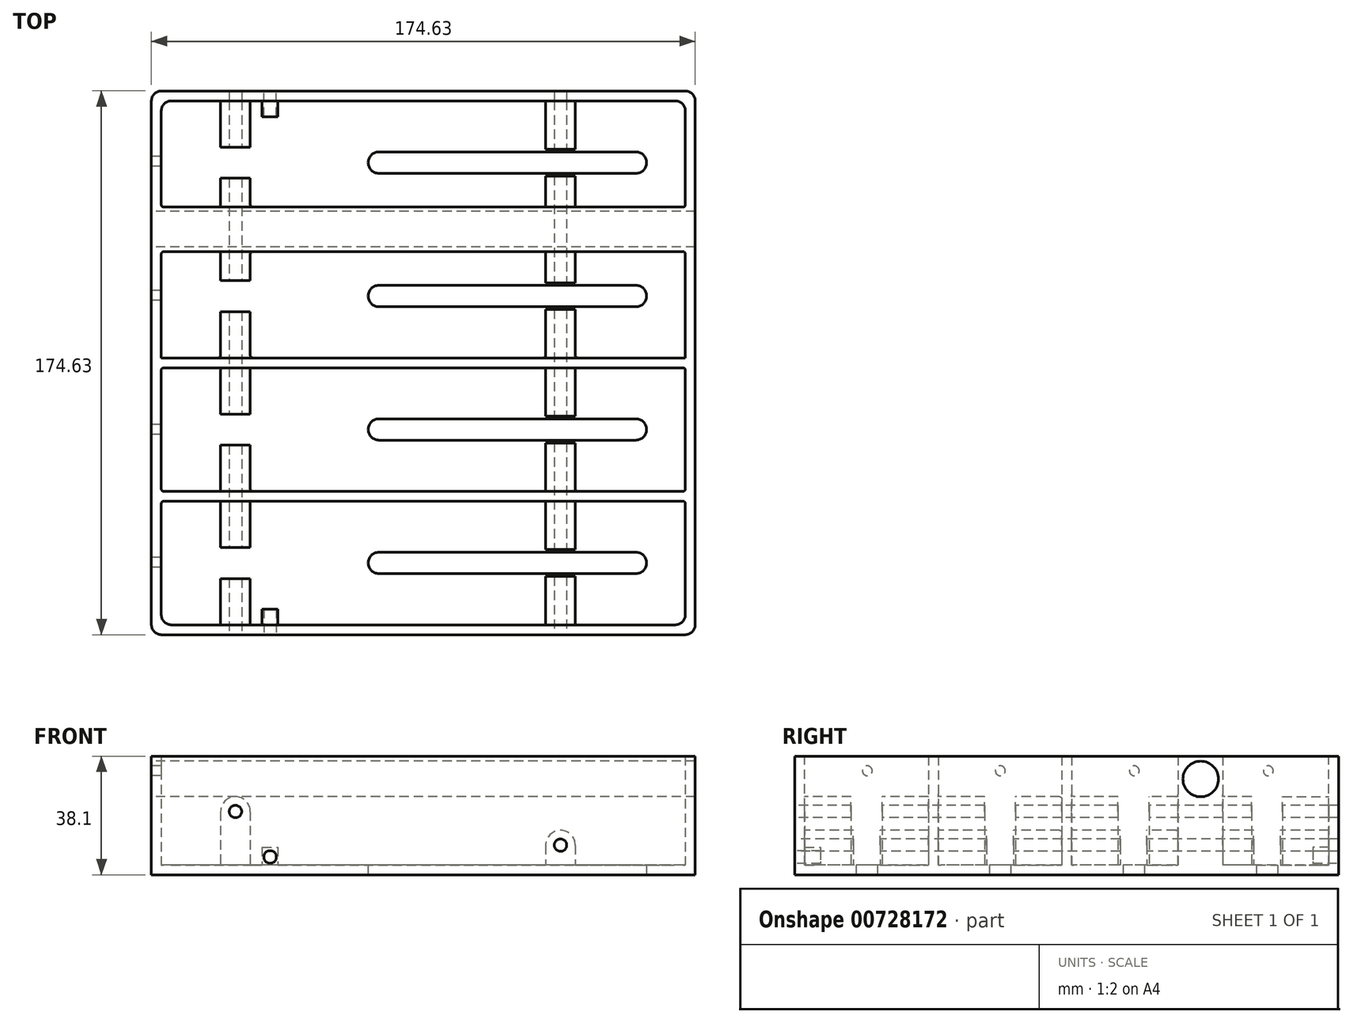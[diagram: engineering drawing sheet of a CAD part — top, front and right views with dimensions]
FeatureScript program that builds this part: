
annotation { "Feature Type Name" : "Feature", "Feature Type Description" : "" }
export const myFeature = defineFeature(function(context is Context, id is Id, definition is map)
    precondition{}
    {
        {
            var Q0;
            Q0=qCreatedBy(makeId("Top.planeOp"),FACE);
            var sketch = newSketch(context, id + "F0", { "sketchPlane" : qUnion([Q0])});
            skLineSegment(sketch, "E0.bottom", {"start": v(0, 0) * mm, "end": v(174.63, 0) * mm});
            skLineSegment(sketch, "E0.top", {"start": v(0, 174.63) * mm, "end": v(174.62, 174.63) * mm});
            skLineSegment(sketch, "E0.left", {"start": v(0, 0) * mm, "end": v(0, 174.63) * mm});
            skLineSegment(sketch, "E0.right", {"start": v(174.63, 0) * mm, "end": v(174.62, 174.63) * mm});
            skSolve(sketch);
        }
        {
            var Q0;
            Q0=qSketchRegion(id+"F0",true);
            extrude(context, id + "F1", {"entities" : qUnion([Q0]), "depth" : 38.1 * mm, "offsetDistance" : 25.4 * mm});
        }
        {
            var Q0;
            Q0=makeQuery(id+"F1.opExtrude","CAP_FACE",FACE,{"disambiguationData":[OSD([sQuery(id+"F0.wireOp",EDGE,"E0.bottom"),sQuery(id+"F0.wireOp",EDGE,"E0.top"),sQuery(id+"F0.wireOp",EDGE,"E0.left"),sQuery(id+"F0.wireOp",EDGE,"E0.right")])],"isStart":false});
            var sketch = newSketch(context, id + "F2", { "sketchPlane" : qUnion([Q0])});
            skLineSegment(sketch, "E1.bottom", {"start": v(3.17, 171.45) * mm, "end": v(171.45, 171.45) * mm});
            skLineSegment(sketch, "E1.top", {"start": v(3.18, 3.18) * mm, "end": v(171.45, 3.18) * mm});
            skLineSegment(sketch, "E1.left", {"start": v(3.17, 171.45) * mm, "end": v(3.18, 3.17) * mm});
            skLineSegment(sketch, "E1.right", {"start": v(171.45, 171.45) * mm, "end": v(171.45, 3.18) * mm});
            skSolve(sketch);
        }
        {
            var Q0;
            Q0=qSketchRegion(id+"F2",true);
            extrude(context, id + "F3", {"entities" : qUnion([Q0]), "operationType" : NewBodyOperationType.REMOVE, "oppositeDirection" : true, "depth" : 34.92 * mm, "offsetDistance" : 25.4 * mm});
        }
        {
            var Q0;
            Q0=makeQuery(id+"F3.boolean.opBoolean","COPY",EDGE,{"derivedFrom":makeQuery(id+"F3.opExtrude","SWEPT_EDGE",EDGE,{"disambiguationData":[OSD([sQuery(id+"F2.wireOp",EDGE,"E1.bottom"),sQuery(id+"F2.wireOp",EDGE,"E1.right")])]})});
            var Q1;
            Q1=makeQuery(id+"F3.boolean.opBoolean","COPY",EDGE,{"derivedFrom":makeQuery(id+"F3.opExtrude","SWEPT_EDGE",EDGE,{"disambiguationData":[OSD([sQuery(id+"F2.wireOp",EDGE,"E1.top"),sQuery(id+"F2.wireOp",EDGE,"E1.right")])]})});
            var Q2;
            Q2=makeQuery(id+"F3.boolean.opBoolean","COPY",EDGE,{"derivedFrom":makeQuery(id+"F3.opExtrude","SWEPT_EDGE",EDGE,{"disambiguationData":[OSD([sQuery(id+"F2.wireOp",EDGE,"E1.bottom"),sQuery(id+"F2.wireOp",EDGE,"E1.left")])]})});
            var Q3;
            Q3=makeQuery(id+"F3.boolean.opBoolean","COPY",EDGE,{"derivedFrom":makeQuery(id+"F3.opExtrude","SWEPT_EDGE",EDGE,{"disambiguationData":[OSD([sQuery(id+"F2.wireOp",EDGE,"E1.top"),sQuery(id+"F2.wireOp",EDGE,"E1.left")])]})});
            var Q4;
            Q4=makeQuery(id+"F1.opExtrude","SWEPT_EDGE",EDGE,{"disambiguationData":[OSD([sQuery(id+"F0.wireOp",EDGE,"E0.top"),sQuery(id+"F0.wireOp",EDGE,"E0.right")])]});
            var Q5;
            Q5=makeQuery(id+"F1.opExtrude","SWEPT_EDGE",EDGE,{"disambiguationData":[OSD([sQuery(id+"F0.wireOp",EDGE,"E0.top"),sQuery(id+"F0.wireOp",EDGE,"E0.left")])]});
            var Q6;
            Q6=makeQuery(id+"F1.opExtrude","SWEPT_EDGE",EDGE,{"disambiguationData":[OSD([sQuery(id+"F0.wireOp",EDGE,"E0.bottom"),sQuery(id+"F0.wireOp",EDGE,"E0.right")])]});
            var Q7;
            Q7=makeQuery(id+"F1.opExtrude","SWEPT_EDGE",EDGE,{"disambiguationData":[OSD([sQuery(id+"F0.wireOp",EDGE,"E0.bottom"),sQuery(id+"F0.wireOp",EDGE,"E0.left")])]});
            fillet(context, id + "F4", {"entities" : qUnion([Q0, Q1, Q2, Q3, Q4, Q5, Q6, Q7]), "radius" : 3.17 * mm, "tangentPropagation" : true, "allowEdgeOverflow" : false});
        }
        {
            var Q0;
            Q0=qCreatedBy(makeId("Top.planeOp"),FACE);
            var sketch = newSketch(context, id + "F5", { "sketchPlane" : qUnion([Q0])});
            skLineSegment(sketch, "E2.bottom", {"start": v(3.36, 131.76) * mm, "end": v(171.33, 131.76) * mm});
            skLineSegment(sketch, "E2.top", {"start": v(3.36, 128.59) * mm, "end": v(171.33, 128.59) * mm});
            skLineSegment(sketch, "E2.left", {"start": v(3.36, 131.76) * mm, "end": v(3.36, 128.59) * mm});
            skLineSegment(sketch, "E2.right", {"start": v(171.33, 131.76) * mm, "end": v(171.33, 128.59) * mm});
            skLineSegment(sketch, "E3.bottom", {"start": v(3.17, 88.9) * mm, "end": v(171.45, 88.9) * mm});
            skLineSegment(sketch, "E3.top", {"start": v(3.17, 85.72) * mm, "end": v(171.45, 85.72) * mm});
            skLineSegment(sketch, "E3.left", {"start": v(3.17, 88.9) * mm, "end": v(3.17, 85.72) * mm});
            skLineSegment(sketch, "E3.right", {"start": v(171.45, 88.9) * mm, "end": v(171.45, 85.73) * mm});
            skLineSegment(sketch, "E4.bottom", {"start": v(3.18, 46.04) * mm, "end": v(171.45, 46.04) * mm});
            skLineSegment(sketch, "E4.top", {"start": v(3.18, 42.86) * mm, "end": v(171.45, 42.86) * mm});
            skLineSegment(sketch, "E4.left", {"start": v(3.18, 46.04) * mm, "end": v(3.18, 42.86) * mm});
            skLineSegment(sketch, "E4.right", {"start": v(171.45, 46.04) * mm, "end": v(171.45, 42.86) * mm});
            skSolve(sketch);
        }
        {
            var Q0;
            Q0=qSketchRegion(id+"F5",true);
            extrude(context, id + "F6", {"entities" : qUnion([Q0]), "operationType" : NewBodyOperationType.ADD, "depth" : 38.1 * mm, "offsetDistance" : 25.4 * mm});
        }
        {
            var Q0;
            Q0=qCreatedBy(makeId("Top.planeOp"),FACE);
            var sketch = newSketch(context, id + "F7", { "sketchPlane" : qUnion([Q0])});
            skLineSegment(sketch, "E5", {"start": v(73.02, 155.03) * mm, "end": v(155.57, 155.03) * mm});
            skArc(sketch, "E6", {"start": v(155.57, 148.17) * mm, "mid": v(159, 151.6) * mm, "end": v(155.57, 155.03) * mm});
            skLineSegment(sketch, "E7", {"start": v(155.57, 148.17) * mm, "end": v(73.02, 148.17) * mm});
            skArc(sketch, "E8", {"start": v(73.02, 155.03) * mm, "mid": v(69.6, 151.6) * mm, "end": v(73.02, 148.17) * mm});
            skLineSegment(sketch, "E9.0.1.0", {"start": v(155.57, 105.32) * mm, "end": v(73.02, 105.32) * mm});
            skArc(sketch, "E9.0.1.1", {"start": v(155.57, 105.32) * mm, "mid": v(159, 108.75) * mm, "end": v(155.57, 112.18) * mm});
            skLineSegment(sketch, "E9.0.1.2", {"start": v(73.02, 112.18) * mm, "end": v(155.57, 112.18) * mm});
            skArc(sketch, "E9.0.1.3", {"start": v(73.02, 112.18) * mm, "mid": v(69.6, 108.75) * mm, "end": v(73.02, 105.32) * mm});
            skLineSegment(sketch, "E9.0.2.0", {"start": v(155.57, 62.47) * mm, "end": v(73.02, 62.47) * mm});
            skArc(sketch, "E9.0.2.1", {"start": v(155.57, 62.47) * mm, "mid": v(159, 65.9) * mm, "end": v(155.57, 69.33) * mm});
            skLineSegment(sketch, "E9.0.2.2", {"start": v(73.02, 69.33) * mm, "end": v(155.57, 69.33) * mm});
            skArc(sketch, "E9.0.2.3", {"start": v(73.02, 69.33) * mm, "mid": v(69.6, 65.9) * mm, "end": v(73.02, 62.47) * mm});
            skLineSegment(sketch, "E9.0.3.0", {"start": v(155.57, 19.62) * mm, "end": v(73.02, 19.62) * mm});
            skArc(sketch, "E9.0.3.1", {"start": v(155.57, 19.62) * mm, "mid": v(159, 23.05) * mm, "end": v(155.57, 26.48) * mm});
            skLineSegment(sketch, "E9.0.3.2", {"start": v(73.02, 26.48) * mm, "end": v(155.57, 26.48) * mm});
            skArc(sketch, "E9.0.3.3", {"start": v(73.02, 26.48) * mm, "mid": v(69.6, 23.05) * mm, "end": v(73.02, 19.62) * mm});
            skLineSegment(sketch, "E9.direction1", {"start": v(73.02, 148.17) * mm, "end": v(73.02, 148.17) * mm});
            skLineSegment(sketch, "E9.direction2", {"start": v(73.02, 148.17) * mm, "end": v(73.02, 105.32) * mm, "construction": true});
            skSolve(sketch);
        }
        {
            var Q0;
            Q0=qSketchRegion(id+"F7",true);
            extrude(context, id + "F8", {"entities" : qUnion([Q0]), "operationType" : NewBodyOperationType.REMOVE, "depth" : 5.08 * mm, "offsetDistance" : 25.4 * mm});
        }
        {
            var Q0;
            Q0=makeQuery(id+"F1.opExtrude","SWEPT_FACE",FACE,{"disambiguationData":[OSD([sQuery(id+"F0.wireOp",EDGE,"E0.bottom")])]});
            var sketch = newSketch(context, id + "F9", { "sketchPlane" : qUnion([Q0])});
            skCircle(sketch, "E10", {"center": v(131.36, 9.53) * mm, "radius": 2 * mm});
            skCircle(sketch, "E11", {"center": v(26.99, 20.32) * mm, "radius": 2 * mm});
            skSolve(sketch);
        }
        {
            var Q0;
            Q0=qCreatedBy(makeId("Top.planeOp"),FACE);
            var sketch = newSketch(context, id + "F10", { "sketchPlane" : qUnion([Q0])});
            skLineSegment(sketch, "E12.bottom", {"start": v(22.23, 3.18) * mm, "end": v(31.75, 3.18) * mm});
            skLineSegment(sketch, "E12.top", {"start": v(22.23, 18.03) * mm, "end": v(31.75, 18.03) * mm});
            skLineSegment(sketch, "E12.left", {"start": v(22.23, 3.18) * mm, "end": v(22.23, 18.03) * mm});
            skLineSegment(sketch, "E12.right", {"start": v(31.75, 3.18) * mm, "end": v(31.75, 18.03) * mm});
            skLineSegment(sketch, "E13.bottom", {"start": v(22.23, 42.86) * mm, "end": v(31.75, 42.86) * mm});
            skLineSegment(sketch, "E13.top", {"start": v(22.23, 28) * mm, "end": v(31.75, 28) * mm});
            skLineSegment(sketch, "E13.left", {"start": v(22.23, 42.86) * mm, "end": v(22.23, 28) * mm});
            skLineSegment(sketch, "E13.right", {"start": v(31.75, 42.86) * mm, "end": v(31.75, 28) * mm});
            skLineSegment(sketch, "E14.0.1.0", {"start": v(31.75, 46.02) * mm, "end": v(31.75, 60.88) * mm});
            skLineSegment(sketch, "E14.0.1.1", {"start": v(22.23, 60.88) * mm, "end": v(31.75, 60.88) * mm});
            skLineSegment(sketch, "E14.0.1.2", {"start": v(22.23, 46.02) * mm, "end": v(22.23, 60.88) * mm});
            skLineSegment(sketch, "E14.0.1.3", {"start": v(22.23, 46.02) * mm, "end": v(31.75, 46.02) * mm});
            skLineSegment(sketch, "E14.0.1.4", {"start": v(22.23, 70.85) * mm, "end": v(31.75, 70.85) * mm});
            skLineSegment(sketch, "E14.0.1.5", {"start": v(31.75, 85.71) * mm, "end": v(31.75, 70.85) * mm});
            skLineSegment(sketch, "E14.0.1.6", {"start": v(22.23, 85.71) * mm, "end": v(22.23, 70.85) * mm});
            skLineSegment(sketch, "E14.0.1.7", {"start": v(22.23, 85.71) * mm, "end": v(31.75, 85.71) * mm});
            skLineSegment(sketch, "E14.0.2.0", {"start": v(31.75, 88.87) * mm, "end": v(31.75, 103.73) * mm});
            skLineSegment(sketch, "E14.0.2.1", {"start": v(22.23, 103.73) * mm, "end": v(31.75, 103.73) * mm});
            skLineSegment(sketch, "E14.0.2.2", {"start": v(22.23, 88.87) * mm, "end": v(22.23, 103.73) * mm});
            skLineSegment(sketch, "E14.0.2.3", {"start": v(22.23, 88.87) * mm, "end": v(31.75, 88.87) * mm});
            skLineSegment(sketch, "E14.0.2.4", {"start": v(22.23, 113.7) * mm, "end": v(31.75, 113.7) * mm});
            skLineSegment(sketch, "E14.0.2.5", {"start": v(31.75, 128.56) * mm, "end": v(31.75, 113.7) * mm});
            skLineSegment(sketch, "E14.0.2.6", {"start": v(22.23, 128.56) * mm, "end": v(22.23, 113.7) * mm});
            skLineSegment(sketch, "E14.0.2.7", {"start": v(22.23, 128.56) * mm, "end": v(31.75, 128.56) * mm});
            skLineSegment(sketch, "E14.0.3.0", {"start": v(31.75, 131.72) * mm, "end": v(31.75, 146.58) * mm});
            skLineSegment(sketch, "E14.0.3.1", {"start": v(22.23, 146.58) * mm, "end": v(31.75, 146.58) * mm});
            skLineSegment(sketch, "E14.0.3.2", {"start": v(22.23, 131.72) * mm, "end": v(22.23, 146.58) * mm});
            skLineSegment(sketch, "E14.0.3.3", {"start": v(22.23, 131.72) * mm, "end": v(31.75, 131.72) * mm});
            skLineSegment(sketch, "E14.0.3.4", {"start": v(22.23, 156.55) * mm, "end": v(31.75, 156.55) * mm});
            skLineSegment(sketch, "E14.0.3.5", {"start": v(31.75, 171.41) * mm, "end": v(31.75, 156.55) * mm});
            skLineSegment(sketch, "E14.0.3.6", {"start": v(22.23, 171.41) * mm, "end": v(22.23, 156.55) * mm});
            skLineSegment(sketch, "E14.0.3.7", {"start": v(22.23, 171.41) * mm, "end": v(31.75, 171.41) * mm});
            skLineSegment(sketch, "E14.direction1", {"start": v(31.75, 3.18) * mm, "end": v(31.75, 3.18) * mm});
            skSolve(sketch);
        }
        {
            var Q0;
            Q0=qSketchRegion(id+"F10",true);
            extrude(context, id + "F11", {"entities" : qUnion([Q0]), "operationType" : NewBodyOperationType.ADD, "depth" : 25.1 * mm, "offsetDistance" : 25.4 * mm});
        }
        {
            var Q0;
            Q0=makeQuery(id+"F11.opExtrude","CAP_EDGE",EDGE,{"disambiguationData":[OSD([sQuery(id+"F10.wireOp",EDGE,"E14.0.3.6")])],"isStart":false});
            var Q1;
            Q1=makeQuery(id+"F11.opExtrude","CAP_EDGE",EDGE,{"disambiguationData":[OSD([sQuery(id+"F10.wireOp",EDGE,"E14.0.3.5")])],"isStart":false});
            var Q2;
            Q2=makeQuery(id+"F11.opExtrude","CAP_EDGE",EDGE,{"disambiguationData":[OSD([sQuery(id+"F10.wireOp",EDGE,"E14.0.3.0")])],"isStart":false});
            var Q3;
            Q3=makeQuery(id+"F11.opExtrude","CAP_EDGE",EDGE,{"disambiguationData":[OSD([sQuery(id+"F10.wireOp",EDGE,"E14.0.3.2")])],"isStart":false});
            var Q4;
            Q4=makeQuery(id+"F11.opExtrude","CAP_EDGE",EDGE,{"disambiguationData":[OSD([sQuery(id+"F10.wireOp",EDGE,"E14.0.2.5")])],"isStart":false});
            var Q5;
            Q5=makeQuery(id+"F11.opExtrude","CAP_EDGE",EDGE,{"disambiguationData":[OSD([sQuery(id+"F10.wireOp",EDGE,"E14.0.2.0")])],"isStart":false});
            var Q6;
            Q6=makeQuery(id+"F11.opExtrude","CAP_EDGE",EDGE,{"disambiguationData":[OSD([sQuery(id+"F10.wireOp",EDGE,"E14.0.1.5")])],"isStart":false});
            var Q7;
            Q7=makeQuery(id+"F11.opExtrude","CAP_EDGE",EDGE,{"disambiguationData":[OSD([sQuery(id+"F10.wireOp",EDGE,"E14.0.1.0")])],"isStart":false});
            var Q8;
            Q8=makeQuery(id+"F11.opExtrude","CAP_EDGE",EDGE,{"disambiguationData":[OSD([sQuery(id+"F10.wireOp",EDGE,"E13.right")])],"isStart":false});
            var Q9;
            Q9=makeQuery(id+"F11.opExtrude","CAP_EDGE",EDGE,{"disambiguationData":[OSD([sQuery(id+"F10.wireOp",EDGE,"E12.right")])],"isStart":false});
            var Q10;
            Q10=makeQuery(id+"F11.opExtrude","CAP_EDGE",EDGE,{"disambiguationData":[OSD([sQuery(id+"F10.wireOp",EDGE,"E14.0.2.6")])],"isStart":false});
            var Q11;
            Q11=makeQuery(id+"F11.opExtrude","CAP_EDGE",EDGE,{"disambiguationData":[OSD([sQuery(id+"F10.wireOp",EDGE,"E14.0.1.6")])],"isStart":false});
            var Q12;
            Q12=makeQuery(id+"F11.opExtrude","CAP_EDGE",EDGE,{"disambiguationData":[OSD([sQuery(id+"F10.wireOp",EDGE,"E14.0.2.2")])],"isStart":false});
            var Q13;
            Q13=makeQuery(id+"F11.opExtrude","CAP_EDGE",EDGE,{"disambiguationData":[OSD([sQuery(id+"F10.wireOp",EDGE,"E14.0.1.2")])],"isStart":false});
            var Q14;
            Q14=makeQuery(id+"F11.opExtrude","CAP_EDGE",EDGE,{"disambiguationData":[OSD([sQuery(id+"F10.wireOp",EDGE,"E13.left")])],"isStart":false});
            var Q15;
            Q15=makeQuery(id+"F11.opExtrude","CAP_EDGE",EDGE,{"disambiguationData":[OSD([sQuery(id+"F10.wireOp",EDGE,"E12.left")])],"isStart":false});
            fillet(context, id + "F12", {"entities" : qUnion([Q0, Q1, Q2, Q3, Q4, Q5, Q6, Q7, Q8, Q9, Q10, Q11, Q12, Q13, Q14, Q15]), "radius" : 4.76 * mm, "tangentPropagation" : true, "allowEdgeOverflow" : false});
        }
        {
            var Q0;
            Q0=makeQuery(id+"F1.opExtrude","CAP_FACE",FACE,{"disambiguationData":[OSD([sQuery(id+"F0.wireOp",EDGE,"E0.bottom"),sQuery(id+"F0.wireOp",EDGE,"E0.top"),sQuery(id+"F0.wireOp",EDGE,"E0.left"),sQuery(id+"F0.wireOp",EDGE,"E0.right")])],"isStart":true});
            var sketch = newSketch(context, id + "F13", { "sketchPlane" : qUnion([Q0])});
            skLineSegment(sketch, "E15.bottom", {"start": v(126.6, -3.18) * mm, "end": v(136.12, -3.18) * mm});
            skLineSegment(sketch, "E15.top", {"start": v(126.6, -18.72) * mm, "end": v(136.12, -18.72) * mm});
            skLineSegment(sketch, "E15.left", {"start": v(126.6, -3.18) * mm, "end": v(126.6, -18.72) * mm});
            skLineSegment(sketch, "E15.right", {"start": v(136.12, -3.18) * mm, "end": v(136.12, -18.72) * mm});
            skLineSegment(sketch, "E16.bottom", {"start": v(126.6, -42.86) * mm, "end": v(136.12, -42.86) * mm});
            skLineSegment(sketch, "E16.top", {"start": v(126.6, -27.32) * mm, "end": v(136.12, -27.32) * mm});
            skLineSegment(sketch, "E16.left", {"start": v(126.6, -42.86) * mm, "end": v(126.6, -27.32) * mm});
            skLineSegment(sketch, "E16.right", {"start": v(136.12, -42.86) * mm, "end": v(136.12, -27.32) * mm});
            skLineSegment(sketch, "E17.0.1.0", {"start": v(136.12, -46.02) * mm, "end": v(136.12, -61.57) * mm});
            skLineSegment(sketch, "E17.0.1.1", {"start": v(126.6, -46.02) * mm, "end": v(136.12, -46.02) * mm});
            skLineSegment(sketch, "E17.0.1.2", {"start": v(126.6, -46.02) * mm, "end": v(126.6, -61.57) * mm});
            skLineSegment(sketch, "E17.0.1.3", {"start": v(126.6, -61.57) * mm, "end": v(136.12, -61.57) * mm});
            skLineSegment(sketch, "E17.0.1.4", {"start": v(136.12, -85.71) * mm, "end": v(136.12, -70.17) * mm});
            skLineSegment(sketch, "E17.0.1.5", {"start": v(126.6, -85.71) * mm, "end": v(126.6, -70.17) * mm});
            skLineSegment(sketch, "E17.0.1.6", {"start": v(126.6, -70.17) * mm, "end": v(136.12, -70.17) * mm});
            skLineSegment(sketch, "E17.0.1.7", {"start": v(126.6, -85.71) * mm, "end": v(136.12, -85.71) * mm});
            skLineSegment(sketch, "E17.0.2.0", {"start": v(136.12, -88.87) * mm, "end": v(136.12, -104.42) * mm});
            skLineSegment(sketch, "E17.0.2.1", {"start": v(126.6, -88.87) * mm, "end": v(136.12, -88.87) * mm});
            skLineSegment(sketch, "E17.0.2.2", {"start": v(126.6, -88.87) * mm, "end": v(126.6, -104.42) * mm});
            skLineSegment(sketch, "E17.0.2.3", {"start": v(126.6, -104.42) * mm, "end": v(136.12, -104.42) * mm});
            skLineSegment(sketch, "E17.0.2.4", {"start": v(136.12, -128.56) * mm, "end": v(136.12, -113.02) * mm});
            skLineSegment(sketch, "E17.0.2.5", {"start": v(126.6, -128.56) * mm, "end": v(126.6, -113.02) * mm});
            skLineSegment(sketch, "E17.0.2.6", {"start": v(126.6, -113.02) * mm, "end": v(136.12, -113.02) * mm});
            skLineSegment(sketch, "E17.0.2.7", {"start": v(126.6, -128.56) * mm, "end": v(136.12, -128.56) * mm});
            skLineSegment(sketch, "E17.0.3.0", {"start": v(136.12, -131.72) * mm, "end": v(136.12, -147.27) * mm});
            skLineSegment(sketch, "E17.0.3.1", {"start": v(126.6, -131.72) * mm, "end": v(136.12, -131.72) * mm});
            skLineSegment(sketch, "E17.0.3.2", {"start": v(126.6, -131.72) * mm, "end": v(126.6, -147.27) * mm});
            skLineSegment(sketch, "E17.0.3.3", {"start": v(126.6, -147.27) * mm, "end": v(136.12, -147.27) * mm});
            skLineSegment(sketch, "E17.0.3.4", {"start": v(136.12, -171.41) * mm, "end": v(136.12, -155.87) * mm});
            skLineSegment(sketch, "E17.0.3.5", {"start": v(126.6, -171.41) * mm, "end": v(126.6, -155.87) * mm});
            skLineSegment(sketch, "E17.0.3.6", {"start": v(126.6, -155.87) * mm, "end": v(136.12, -155.87) * mm});
            skLineSegment(sketch, "E17.0.3.7", {"start": v(126.6, -171.41) * mm, "end": v(136.12, -171.41) * mm});
            skLineSegment(sketch, "E17.direction1", {"start": v(136.12, -18.72) * mm, "end": v(161.52, -18.72) * mm, "construction": true});
            skLineSegment(sketch, "E17.direction2", {"start": v(136.12, -18.72) * mm, "end": v(136.12, -61.57) * mm, "construction": true});
            skSolve(sketch);
        }
        {
            var Q0;
            Q0=qSketchRegion(id+"F13",true);
            extrude(context, id + "F14", {"entities" : qUnion([Q0]), "operationType" : NewBodyOperationType.ADD, "oppositeDirection" : true, "depth" : 14.29 * mm, "offsetDistance" : 25.4 * mm});
        }
        {
            var Q0;
            Q0=makeQuery(id+"F14.opExtrude","CAP_EDGE",EDGE,{"disambiguationData":[OSD([sQuery(id+"F13.wireOp",EDGE,"E17.0.3.5")])],"isStart":false});
            var Q1;
            Q1=makeQuery(id+"F14.opExtrude","CAP_EDGE",EDGE,{"disambiguationData":[OSD([sQuery(id+"F13.wireOp",EDGE,"E17.0.3.2")])],"isStart":false});
            var Q2;
            Q2=makeQuery(id+"F14.opExtrude","CAP_EDGE",EDGE,{"disambiguationData":[OSD([sQuery(id+"F13.wireOp",EDGE,"E17.0.2.5")])],"isStart":false});
            var Q3;
            Q3=makeQuery(id+"F14.opExtrude","CAP_EDGE",EDGE,{"disambiguationData":[OSD([sQuery(id+"F13.wireOp",EDGE,"E17.0.2.2")])],"isStart":false});
            var Q4;
            Q4=makeQuery(id+"F14.opExtrude","CAP_EDGE",EDGE,{"disambiguationData":[OSD([sQuery(id+"F13.wireOp",EDGE,"E17.0.1.5")])],"isStart":false});
            var Q5;
            Q5=makeQuery(id+"F14.opExtrude","CAP_EDGE",EDGE,{"disambiguationData":[OSD([sQuery(id+"F13.wireOp",EDGE,"E17.0.1.2")])],"isStart":false});
            var Q6;
            Q6=makeQuery(id+"F14.opExtrude","CAP_EDGE",EDGE,{"disambiguationData":[OSD([sQuery(id+"F13.wireOp",EDGE,"E16.left")])],"isStart":false});
            var Q7;
            Q7=makeQuery(id+"F14.opExtrude","CAP_EDGE",EDGE,{"disambiguationData":[OSD([sQuery(id+"F13.wireOp",EDGE,"E15.left")])],"isStart":false});
            var Q8;
            Q8=makeQuery(id+"F14.opExtrude","CAP_EDGE",EDGE,{"disambiguationData":[OSD([sQuery(id+"F13.wireOp",EDGE,"E15.right")])],"isStart":false});
            var Q9;
            Q9=makeQuery(id+"F14.opExtrude","CAP_EDGE",EDGE,{"disambiguationData":[OSD([sQuery(id+"F13.wireOp",EDGE,"E16.right")])],"isStart":false});
            var Q10;
            Q10=makeQuery(id+"F14.opExtrude","CAP_EDGE",EDGE,{"disambiguationData":[OSD([sQuery(id+"F13.wireOp",EDGE,"E17.0.1.0")])],"isStart":false});
            var Q11;
            Q11=makeQuery(id+"F14.opExtrude","CAP_EDGE",EDGE,{"disambiguationData":[OSD([sQuery(id+"F13.wireOp",EDGE,"E17.0.1.4")])],"isStart":false});
            var Q12;
            Q12=makeQuery(id+"F14.opExtrude","CAP_EDGE",EDGE,{"disambiguationData":[OSD([sQuery(id+"F13.wireOp",EDGE,"E17.0.2.0")])],"isStart":false});
            var Q13;
            Q13=makeQuery(id+"F14.opExtrude","CAP_EDGE",EDGE,{"disambiguationData":[OSD([sQuery(id+"F13.wireOp",EDGE,"E17.0.2.4")])],"isStart":false});
            var Q14;
            Q14=makeQuery(id+"F14.opExtrude","CAP_EDGE",EDGE,{"disambiguationData":[OSD([sQuery(id+"F13.wireOp",EDGE,"E17.0.3.0")])],"isStart":false});
            var Q15;
            Q15=makeQuery(id+"F14.opExtrude","CAP_EDGE",EDGE,{"disambiguationData":[OSD([sQuery(id+"F13.wireOp",EDGE,"E17.0.3.4")])],"isStart":false});
            fillet(context, id + "F15", {"entities" : qUnion([Q0, Q1, Q2, Q3, Q4, Q5, Q6, Q7, Q8, Q9, Q10, Q11, Q12, Q13, Q14, Q15]), "radius" : 4.76 * mm, "tangentPropagation" : true, "allowEdgeOverflow" : false});
        }
        {
            var Q0;
            Q0=makeQuery(id+"F1.opExtrude","SWEPT_FACE",FACE,{"disambiguationData":[OSD([sQuery(id+"F0.wireOp",EDGE,"E0.bottom")])]});
            var sketch = newSketch(context, id + "F16", { "sketchPlane" : qUnion([Q0])});
            skCircle(sketch, "E18", {"center": v(38.1, 5.72) * mm, "radius": 2.02 * mm});
            skSolve(sketch);
        }
        {
            var Q0;
            Q0=qCreatedBy(makeId("Top.planeOp"),FACE);
            var sketch = newSketch(context, id + "F17", { "sketchPlane" : qUnion([Q0])});
            skLineSegment(sketch, "E19.bottom", {"start": v(2.63, 137.31) * mm, "end": v(173.93, 137.31) * mm});
            skLineSegment(sketch, "E19.top", {"start": v(2.63, 123.02) * mm, "end": v(173.93, 123.02) * mm});
            skLineSegment(sketch, "E19.left", {"start": v(2.63, 137.31) * mm, "end": v(2.63, 123.02) * mm});
            skLineSegment(sketch, "E19.right", {"start": v(173.93, 137.31) * mm, "end": v(173.93, 123.02) * mm});
            skSolve(sketch);
        }
        {
            var Q0;
            Q0=qSketchRegion(id+"F17",true);
            extrude(context, id + "F18", {"entities" : qUnion([Q0]), "operationType" : NewBodyOperationType.ADD, "depth" : 38.1 * mm, "offsetDistance" : 25.4 * mm});
        }
        {
            var Q0;
            Q0=makeQuery(id+"F84Vj0c6t74moK0_1.boolean.opBoolean","INTERSECT",EDGE,{"derivedFrom":[makeQuery(id+"F11.opExtrude","SWEPT_FACE",FACE,{"disambiguationData":[OSD([sQuery(id+"F10.wireOp",EDGE,"E14.0.3.5")])]}),makeQuery(id+"F84Vj0c6t74moK0_1.opExtrude","SWEPT_FACE",FACE,{"disambiguationData":[OSD([sQuery(id+"F7s0Sf0SolTK1rK_1.wireOp",EDGE,"r1cm2eqP-3PlX-OLfA-6lGh-JMt8esORfRlw.top")])]})]});
            var Q1;
            Q1=makeQuery(id+"F84Vj0c6t74moK0_1.boolean.opBoolean","INTERSECT",EDGE,{"derivedFrom":[makeQuery(id+"F14.opExtrude","SWEPT_FACE",FACE,{"disambiguationData":[OSD([sQuery(id+"F13.wireOp",EDGE,"E17.0.3.4")])]}),makeQuery(id+"F84Vj0c6t74moK0_1.opExtrude","SWEPT_FACE",FACE,{"disambiguationData":[OSD([sQuery(id+"F7s0Sf0SolTK1rK_1.wireOp",EDGE,"r1cm2eqP-3PlX-OLfA-6lGh-JMt8esORfRlw.top")])]})]});
            var Q2;
            Q2=makeQuery(id+"F84Vj0c6t74moK0_1.boolean.opBoolean","INTERSECT",EDGE,{"derivedFrom":[makeQuery(id+"F15.opFillet","BLEND_FACE",FACE,{"disambiguationData":[OSD([sQuery(id+"F13.wireOp",EDGE,"E17.0.3.5")])]}),makeQuery(id+"F84Vj0c6t74moK0_1.opExtrude","SWEPT_FACE",FACE,{"disambiguationData":[OSD([sQuery(id+"F7s0Sf0SolTK1rK_1.wireOp",EDGE,"r1cm2eqP-3PlX-OLfA-6lGh-JMt8esORfRlw.top")])]})]});
            var Q3;
            Q3=makeQuery(id+"F84Vj0c6t74moK0_1.boolean.opBoolean","INTERSECT",EDGE,{"derivedFrom":[makeQuery(id+"F14.opExtrude","SWEPT_FACE",FACE,{"disambiguationData":[OSD([sQuery(id+"F13.wireOp",EDGE,"E17.0.3.5")])]}),makeQuery(id+"F84Vj0c6t74moK0_1.opExtrude","SWEPT_FACE",FACE,{"disambiguationData":[OSD([sQuery(id+"F7s0Sf0SolTK1rK_1.wireOp",EDGE,"r1cm2eqP-3PlX-OLfA-6lGh-JMt8esORfRlw.top")])]})]});
            var Q4;
            Q4=makeQuery(id+"F18.boolean.opBoolean","INTERSECT",EDGE,{"derivedFrom":[makeQuery(id+"F11.opExtrude","SWEPT_FACE",FACE,{"disambiguationData":[OSD([sQuery(id+"F10.wireOp",EDGE,"E14.0.3.0")])]}),makeQuery(id+"F18.opExtrude","SWEPT_FACE",FACE,{"disambiguationData":[OSD([sQuery(id+"F17.wireOp",EDGE,"E19.bottom")])]})]});
            var Q5;
            Q5=makeQuery(id+"F18.boolean.opBoolean","INTERSECT",EDGE,{"derivedFrom":[makeQuery(id+"F14.opExtrude","SWEPT_FACE",FACE,{"disambiguationData":[OSD([sQuery(id+"F13.wireOp",EDGE,"E17.0.3.2")])]}),makeQuery(id+"F18.opExtrude","SWEPT_FACE",FACE,{"disambiguationData":[OSD([sQuery(id+"F17.wireOp",EDGE,"E19.bottom")])]})]});
            var Q6;
            Q6=makeQuery(id+"F18.boolean.opBoolean","INTERSECT",EDGE,{"derivedFrom":[makeQuery(id+"F11.opExtrude","SWEPT_FACE",FACE,{"disambiguationData":[OSD([sQuery(id+"F10.wireOp",EDGE,"E14.0.2.5")])]}),makeQuery(id+"F18.opExtrude","SWEPT_FACE",FACE,{"disambiguationData":[OSD([sQuery(id+"F17.wireOp",EDGE,"E19.top")])]})]});
            var Q7;
            Q7=makeQuery(id+"F18.boolean.opBoolean","INTERSECT",EDGE,{"derivedFrom":[makeQuery(id+"F14.opExtrude","SWEPT_FACE",FACE,{"disambiguationData":[OSD([sQuery(id+"F13.wireOp",EDGE,"E17.0.2.4")])]}),makeQuery(id+"F18.opExtrude","SWEPT_FACE",FACE,{"disambiguationData":[OSD([sQuery(id+"F17.wireOp",EDGE,"E19.top")])]})]});
            var Q8;
            Q8=makeQuery(id+"F14.opExtrude","SWEPT_EDGE",EDGE,{"disambiguationData":[OSD([sQuery(id+"F13.wireOp",EDGE,"E17.0.1.4"),sQuery(id+"F13.wireOp",EDGE,"E17.0.1.7")])]});
            var Q9;
            Q9=makeQuery(id+"F11.opExtrude","SWEPT_EDGE",EDGE,{"disambiguationData":[OSD([sQuery(id+"F10.wireOp",EDGE,"E14.0.1.5"),sQuery(id+"F10.wireOp",EDGE,"E14.0.1.7")])]});
            var Q10;
            Q10=makeQuery(id+"F11.opExtrude","SWEPT_EDGE",EDGE,{"disambiguationData":[OSD([sQuery(id+"F10.wireOp",EDGE,"E13.bottom"),sQuery(id+"F10.wireOp",EDGE,"E13.right")])]});
            var Q11;
            Q11=makeQuery(id+"F14.opExtrude","SWEPT_EDGE",EDGE,{"disambiguationData":[OSD([sQuery(id+"F13.wireOp",EDGE,"E16.bottom"),sQuery(id+"F13.wireOp",EDGE,"E16.right")])]});
            var Q12;
            Q12=makeQuery(id+"F6.opExtrude","SWEPT_EDGE",EDGE,{"disambiguationData":[OSD([sQuery(id+"F5.wireOp",EDGE,"E4.top"),sQuery(id+"F5.wireOp",EDGE,"E4.left")])]});
            var Q13;
            Q13=makeQuery(id+"F6.opExtrude","SWEPT_EDGE",EDGE,{"disambiguationData":[OSD([sQuery(id+"F5.wireOp",EDGE,"E3.top"),sQuery(id+"F5.wireOp",EDGE,"E3.left")])]});
            var Q14;
            Q14=makeQuery(id+"F18.boolean.opBoolean","INTERSECT",EDGE,{"derivedFrom":[makeQuery(id+"F3.boolean.opBoolean","COPY",FACE,{"derivedFrom":makeQuery(id+"F3.opExtrude","SWEPT_FACE",FACE,{"disambiguationData":[OSD([sQuery(id+"F2.wireOp",EDGE,"E1.left")])]})}),makeQuery(id+"F18.opExtrude","SWEPT_FACE",FACE,{"disambiguationData":[OSD([sQuery(id+"F17.wireOp",EDGE,"E19.top")])]})]});
            var Q15;
            {var subQ0=sQuery(id+"F2.wireOp",EDGE,"E1.right");Q15=makeQuery(id+"F4.opFillet","BLEND_EDGE",EDGE,{"blendedFrom":[makeQuery(id+"F3.boolean.opBoolean","COPY",EDGE,{"derivedFrom":makeQuery(id+"F3.opExtrude","SWEPT_EDGE",EDGE,{"disambiguationData":[OSD([sQuery(id+"F2.wireOp",EDGE,"E1.bottom"),subQ0])]})}),makeQuery(id+"F3.boolean.opBoolean","COPY",FACE,{"derivedFrom":makeQuery(id+"F3.opExtrude","SWEPT_FACE",FACE,{"disambiguationData":[OSD([subQ0])]})})],"blendedInto":[makeQuery(id+"F3.boolean.opBoolean","COPY",FACE,{"derivedFrom":makeQuery(id+"F3.opExtrude","SWEPT_FACE",FACE,{"disambiguationData":[OSD([subQ0])]})})]});}
            var Q16;
            Q16=makeQuery(id+"F18.boolean.opBoolean","INTERSECT",EDGE,{"derivedFrom":[makeQuery(id+"F3.boolean.opBoolean","COPY",FACE,{"derivedFrom":makeQuery(id+"F3.opExtrude","SWEPT_FACE",FACE,{"disambiguationData":[OSD([sQuery(id+"F2.wireOp",EDGE,"E1.right")])]})}),makeQuery(id+"F18.opExtrude","SWEPT_FACE",FACE,{"disambiguationData":[OSD([sQuery(id+"F17.wireOp",EDGE,"E19.top")])]})]});
            var Q17;
            Q17=makeQuery(id+"F6.opExtrude","SWEPT_EDGE",EDGE,{"disambiguationData":[OSD([sQuery(id+"F5.wireOp",EDGE,"E3.top"),sQuery(id+"F5.wireOp",EDGE,"E3.right")])]});
            var Q18;
            Q18=makeQuery(id+"F6.opExtrude","SWEPT_EDGE",EDGE,{"disambiguationData":[OSD([sQuery(id+"F5.wireOp",EDGE,"E4.top"),sQuery(id+"F5.wireOp",EDGE,"E4.right")])]});
            var Q19;
            Q19=makeQuery(id+"F14.boolean.opBoolean","INTERSECT",EDGE,{"derivedFrom":[makeQuery(id+"F6.opExtrude","SWEPT_FACE",FACE,{"disambiguationData":[OSD([sQuery(id+"F5.wireOp",EDGE,"E3.bottom")])]}),makeQuery(id+"F14.opExtrude","SWEPT_FACE",FACE,{"disambiguationData":[OSD([sQuery(id+"F13.wireOp",EDGE,"E17.0.2.0")])]})]});
            var Q20;
            Q20=makeQuery(id+"F11.boolean.opBoolean","INTERSECT",EDGE,{"derivedFrom":[makeQuery(id+"F6.opExtrude","SWEPT_FACE",FACE,{"disambiguationData":[OSD([sQuery(id+"F5.wireOp",EDGE,"E3.bottom")])]}),makeQuery(id+"F11.opExtrude","SWEPT_FACE",FACE,{"disambiguationData":[OSD([sQuery(id+"F10.wireOp",EDGE,"E14.0.2.0")])]})]});
            var Q21;
            Q21=makeQuery(id+"F11.boolean.opBoolean","INTERSECT",EDGE,{"derivedFrom":[makeQuery(id+"F6.opExtrude","SWEPT_FACE",FACE,{"disambiguationData":[OSD([sQuery(id+"F5.wireOp",EDGE,"E4.bottom")])]}),makeQuery(id+"F11.opExtrude","SWEPT_FACE",FACE,{"disambiguationData":[OSD([sQuery(id+"F10.wireOp",EDGE,"E14.0.1.0")])]})]});
            var Q22;
            Q22=makeQuery(id+"F14.boolean.opBoolean","INTERSECT",EDGE,{"derivedFrom":[makeQuery(id+"F6.opExtrude","SWEPT_FACE",FACE,{"disambiguationData":[OSD([sQuery(id+"F5.wireOp",EDGE,"E4.bottom")])]}),makeQuery(id+"F14.opExtrude","SWEPT_FACE",FACE,{"disambiguationData":[OSD([sQuery(id+"F13.wireOp",EDGE,"E17.0.1.0")])]})]});
            var Q23;
            Q23=makeQuery(id+"F14.opExtrude","SWEPT_EDGE",EDGE,{"disambiguationData":[OSD([sQuery(id+"F13.wireOp",EDGE,"E15.bottom"),sQuery(id+"F13.wireOp",EDGE,"E15.right")])]});
            var Q24;
            Q24=makeQuery(id+"F11.opExtrude","SWEPT_EDGE",EDGE,{"disambiguationData":[OSD([sQuery(id+"F10.wireOp",EDGE,"E12.bottom"),sQuery(id+"F10.wireOp",EDGE,"E12.right")])]});
            var Q25;
            Q25=makeQuery(id+"F6.opExtrude","SWEPT_EDGE",EDGE,{"disambiguationData":[OSD([sQuery(id+"F5.wireOp",EDGE,"E4.bottom"),sQuery(id+"F5.wireOp",EDGE,"E4.left")])]});
            var Q26;
            Q26=makeQuery(id+"F6.opExtrude","SWEPT_EDGE",EDGE,{"disambiguationData":[OSD([sQuery(id+"F5.wireOp",EDGE,"E3.bottom"),sQuery(id+"F5.wireOp",EDGE,"E3.left")])]});
            var Q27;
            Q27=makeQuery(id+"F6.opExtrude","SWEPT_EDGE",EDGE,{"disambiguationData":[OSD([sQuery(id+"F5.wireOp",EDGE,"E4.bottom"),sQuery(id+"F5.wireOp",EDGE,"E4.right")])]});
            var Q28;
            Q28=makeQuery(id+"F6.opExtrude","SWEPT_EDGE",EDGE,{"disambiguationData":[OSD([sQuery(id+"F5.wireOp",EDGE,"E3.bottom"),sQuery(id+"F5.wireOp",EDGE,"E3.right")])]});
            var Q29;
            Q29=makeQuery(id+"F18.boolean.opBoolean","INTERSECT",EDGE,{"derivedFrom":[makeQuery(id+"F3.boolean.opBoolean","COPY",FACE,{"derivedFrom":makeQuery(id+"F3.opExtrude","SWEPT_FACE",FACE,{"disambiguationData":[OSD([sQuery(id+"F2.wireOp",EDGE,"E1.right")])]})}),makeQuery(id+"F18.opExtrude","SWEPT_FACE",FACE,{"disambiguationData":[OSD([sQuery(id+"F17.wireOp",EDGE,"E19.bottom")])]})]});
            var Q30;
            {var subQ0=sQuery(id+"F2.wireOp",EDGE,"E1.left");Q30=makeQuery(id+"F4.opFillet","BLEND_EDGE",EDGE,{"blendedFrom":[makeQuery(id+"F3.boolean.opBoolean","COPY",EDGE,{"derivedFrom":makeQuery(id+"F3.opExtrude","SWEPT_EDGE",EDGE,{"disambiguationData":[OSD([sQuery(id+"F2.wireOp",EDGE,"E1.bottom"),subQ0])]})}),makeQuery(id+"F3.boolean.opBoolean","COPY",FACE,{"derivedFrom":makeQuery(id+"F3.opExtrude","SWEPT_FACE",FACE,{"disambiguationData":[OSD([subQ0])]})})],"blendedInto":[makeQuery(id+"F3.boolean.opBoolean","COPY",FACE,{"derivedFrom":makeQuery(id+"F3.opExtrude","SWEPT_FACE",FACE,{"disambiguationData":[OSD([subQ0])]})})]});}
            var Q31;
            Q31=makeQuery(id+"F18.boolean.opBoolean","INTERSECT",EDGE,{"derivedFrom":[makeQuery(id+"F3.boolean.opBoolean","COPY",FACE,{"derivedFrom":makeQuery(id+"F3.opExtrude","SWEPT_FACE",FACE,{"disambiguationData":[OSD([sQuery(id+"F2.wireOp",EDGE,"E1.left")])]})}),makeQuery(id+"F18.opExtrude","SWEPT_FACE",FACE,{"disambiguationData":[OSD([sQuery(id+"F17.wireOp",EDGE,"E19.bottom")])]})]});
            fillet(context, id + "F19", {"entities" : qUnion([Q0, Q1, Q2, Q3, Q4, Q5, Q6, Q7, Q8, Q9, Q10, Q11, Q12, Q13, Q14, Q15, Q16, Q17, Q18, Q19, Q20, Q21, Q22, Q23, Q24, Q25, Q26, Q27, Q28, Q29, Q30, Q31]), "radius" : 0.76 * mm, "tangentPropagation" : true, "allowEdgeOverflow" : false});
        }
        {
            var Q0;
            Q0=makeQuery(id+"F1.opExtrude","SWEPT_FACE",FACE,{"disambiguationData":[OSD([sQuery(id+"F0.wireOp",EDGE,"E0.left")])]});
            var sketch = newSketch(context, id + "F20", { "sketchPlane" : qUnion([Q0])});
            skCircle(sketch, "E20", {"center": v(-130.28, 30.75) * mm, "radius": 5.72 * mm});
            skSolve(sketch);
        }
        {
            var Q0;
            Q0=qSketchRegion(id+"F20",true);
            extrude(context, id + "F21", {"entities" : qUnion([Q0]), "operationType" : NewBodyOperationType.REMOVE, "oppositeDirection" : true, "depth" : 177.8 * mm, "offsetDistance" : 25.4 * mm});
        }
        {
            var Q0;
            Q0=makeQuery(id+"F84Vj0c6t74moK0_1.boolean.opBoolean","MERGE",FACE,{"derivedFrom":[makeQuery(id+"F1.opExtrude","CAP_FACE",FACE,{"disambiguationData":[OSD([sQuery(id+"F0.wireOp",EDGE,"E0.bottom"),sQuery(id+"F0.wireOp",EDGE,"E0.top"),sQuery(id+"F0.wireOp",EDGE,"E0.left"),sQuery(id+"F0.wireOp",EDGE,"E0.right")])],"isStart":true}),makeQuery(id+"F84Vj0c6t74moK0_1.opExtrude","CAP_FACE",FACE,{"disambiguationData":[OSD([sQuery(id+"F7s0Sf0SolTK1rK_1.wireOp",EDGE,"r1cm2eqP-3PlX-OLfA-6lGh-JMt8esORfRlw.bottom"),sQuery(id+"F7s0Sf0SolTK1rK_1.wireOp",EDGE,"r1cm2eqP-3PlX-OLfA-6lGh-JMt8esORfRlw.top"),sQuery(id+"F7s0Sf0SolTK1rK_1.wireOp",EDGE,"r1cm2eqP-3PlX-OLfA-6lGh-JMt8esORfRlw.left"),sQuery(id+"F7s0Sf0SolTK1rK_1.wireOp",EDGE,"r1cm2eqP-3PlX-OLfA-6lGh-JMt8esORfRlw.right")])],"isStart":true})]});
            var sketch = newSketch(context, id + "F22", { "sketchPlane" : qUnion([Q0])});
            skLineSegment(sketch, "E21.bottom", {"start": v(35.56, -3.18) * mm, "end": v(40.64, -3.18) * mm});
            skLineSegment(sketch, "E21.top", {"start": v(35.56, -8.26) * mm, "end": v(40.64, -8.26) * mm});
            skLineSegment(sketch, "E21.left", {"start": v(35.56, -3.18) * mm, "end": v(35.56, -8.26) * mm});
            skLineSegment(sketch, "E21.right", {"start": v(40.64, -3.18) * mm, "end": v(40.64, -8.26) * mm});
            skLineSegment(sketch, "E22.bottom", {"start": v(35.56, -171.45) * mm, "end": v(40.64, -171.45) * mm});
            skLineSegment(sketch, "E22.top", {"start": v(35.56, -166.37) * mm, "end": v(40.64, -166.37) * mm});
            skLineSegment(sketch, "E22.left", {"start": v(35.56, -171.45) * mm, "end": v(35.56, -166.37) * mm});
            skLineSegment(sketch, "E22.right", {"start": v(40.64, -171.45) * mm, "end": v(40.64, -166.37) * mm});
            skSolve(sketch);
        }
        {
            var Q0;
            Q0=qSketchRegion(id+"F22",true);
            extrude(context, id + "F23", {"entities" : qUnion([Q0]), "operationType" : NewBodyOperationType.ADD, "oppositeDirection" : true, "depth" : 8.9 * mm, "offsetDistance" : 25.4 * mm});
        }
        {
            var Q0;
            Q0=qSketchRegion(id+"F16",true);
            extrude(context, id + "F24", {"entities" : qUnion([Q0]), "operationType" : NewBodyOperationType.REMOVE, "oppositeDirection" : true, "depth" : 8.9 * mm, "offsetDistance" : 25.4 * mm});
        }
        {
            var Q0;
            Q0=qSketchRegion(id+"F9",true);
            extrude(context, id + "F25", {"entities" : qUnion([Q0]), "operationType" : NewBodyOperationType.REMOVE, "oppositeDirection" : true, "depth" : 177.8 * mm, "offsetDistance" : 25.4 * mm});
        }
        {
            var Q0;
            Q0=makeQuery(id+"F1.opExtrude","SWEPT_FACE",FACE,{"disambiguationData":[OSD([sQuery(id+"F0.wireOp",EDGE,"E0.left")])]});
            var sketch = newSketch(context, id + "F26", { "sketchPlane" : qUnion([Q0])});
            skCircle(sketch, "E23", {"center": v(-151.99, 33.38) * mm, "radius": 1.59 * mm});
            skCircle(sketch, "E24", {"center": v(-108.97, 33.38) * mm, "radius": 1.59 * mm});
            skCircle(sketch, "E25", {"center": v(-65.96, 33.38) * mm, "radius": 1.59 * mm});
            skCircle(sketch, "E26", {"center": v(-23.25, 33.38) * mm, "radius": 1.59 * mm});
            skSolve(sketch);
        }
        {
            var Q0;
            Q0=qSketchRegion(id+"F26",true);
            extrude(context, id + "F27", {"entities" : qUnion([Q0]), "operationType" : NewBodyOperationType.REMOVE, "oppositeDirection" : true, "depth" : 5.08 * mm, "offsetDistance" : 25.4 * mm});
        }
        {
            var Q0;
            Q0=makeQuery(id+"F1.opExtrude","SWEPT_FACE",FACE,{"disambiguationData":[OSD([sQuery(id+"F0.wireOp",EDGE,"E0.top")])]});
            var sketch = newSketch(context, id + "F28", { "sketchPlane" : qUnion([Q0])});
            skCircle(sketch, "E27", {"center": v(-38.1, 5.73) * mm, "radius": 2.02 * mm});
            skSolve(sketch);
        }
        {
            var Q0;
            Q0 = qSketchRegion(id + "F28", true);
            extrude(context, id + "F29", {"entities" : qUnion([Q0]), "operationType" : NewBodyOperationType.REMOVE, "oppositeDirection" : true, "depth" : 8.28 * mm, "offsetDistance" : 25.4 * mm});
        }
    });
